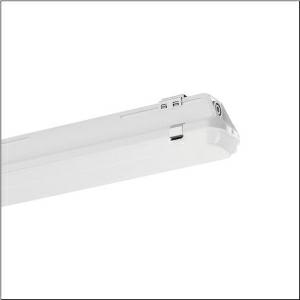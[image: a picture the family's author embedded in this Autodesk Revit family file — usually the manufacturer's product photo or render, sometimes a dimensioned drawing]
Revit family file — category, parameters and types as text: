
# Revit family: monsun_r__21_emergency_51fb107l447k3g_6241
name_source: partatom
category: Lighting Fixtures
units: mm (PartAtom-declared; Revit-internal decimal feet)

## family parameters
Cut with Voids When Loaded = No
Host = Face
Light Source = No
Part Type = Normal
Room Calculation Point = No
Round Connector Dimension = Use Diameter
Shared = No

## types (1)
- --- (1 x LED, 4330 lm, 28.8 W, 4000K)
    Apparent Load = 29 VA
    CIE Flux Codes = 46 76 93 94 100
    Color Rendering = 80
    Color Temperature = 4000K
    Default Elevation = 1800 mm
    Description = Monsun® 21 emergency, damp-proof luminaire, chain hanger, primary optical cover: enclosure, of PMMA, light emission: direct distribution, primary light characteristic: symmetric, installation type: suspended mounting, surface-mounted, horizontal mounting, vertical mounting, LED, rated luminous flux: 4.330lm, luminous efficacy: 173lm/W, light colour: 840, colour temperature: 4000K, control gear: ON/OFF, with terminal, 3-pole, max. 2.5mm², mains connection: 220..240V, AC, 50/60Hz, rated input power: 29W, control gear: single battery element, battery: LiFePO4, 9Ah, housing, of glass-fibre reinforced plastic, uncoated, bright grey, incl. chain hanger, length: 1.299mm, width: 90mm, height: 88mm, clip for enclosure, of stainless steel (V2A), ceiling mounting element, of stainless steel (V2A), chain hanger, of stainless steel (V2A), protection rating (complete): IP66, insulation class (complete): insulation class I (protective earthing), certification: CE, UKCA, protection symbol: D, impact resistance: IK04, permissible operating ambient temperature: +5..+25°C, standard: EN 50419, EN 60598-2-1, corresponds to IFS (International Featured Standards) requirements for safety and quality in the food industry, for indoor or canopied outdoor use, no direct snow, no direct sun, no direct rain, LABS conformity tested according to VDMA 24364:2018-05, contact your sales advisor before using the luminaires in applications with unclear chemical exposure, large temperature fluctuations or condensation-forming humidity, packaging unit: 1 piece
    Height = 88 mm
    Lamp = 1 x LED
    Lamp Light Flux = 4330 lm
    Lamp Power = 28.8 W
    Lamp count = 1
    Length = 1299 mm
    Luminous efficacy = 150 lm/W
    Manufacturer = Siteco
    ModVariant = No
    Model = 51FB107L447K3G
    Mounting Place = Ceiling
    Mounting Type = Surface mounted
    Number of Poles = 1
    OnlyDefault = Yes
    Power Factor = 1
    Product Name = Monsun® 21 emergency
    Product group = damp-proof luminaire
    ProductGroupID = 301
    Protection Class = Protection class I
    Protection Degree = IP 66
    RLX_Detail_Level = 1
    RLX_Emergency_Light_Flux = 0 lm
    RLX_Emergency_Type = 0
    RLX_Emergency_Type_DB = No
    RlxData = <blob elided: 90069 chars, md5=9dfbfcdb>
    Socket = socket
    Standby Power = 0 W
    System Light Flux = 4330 lm
    System Power = 29 W
    Type Comments = -
    Type Image = l_1319656.jpg
    URL = http://relux.com
    VarID = @adj_041147
    Voltage = 0 V
    Weight = 0.00 kg
    Width = 90 mm

## geometry (parser evidence)
native form markers: Blend x4, Sweep x15
no freeform markers — native parametric forms only
